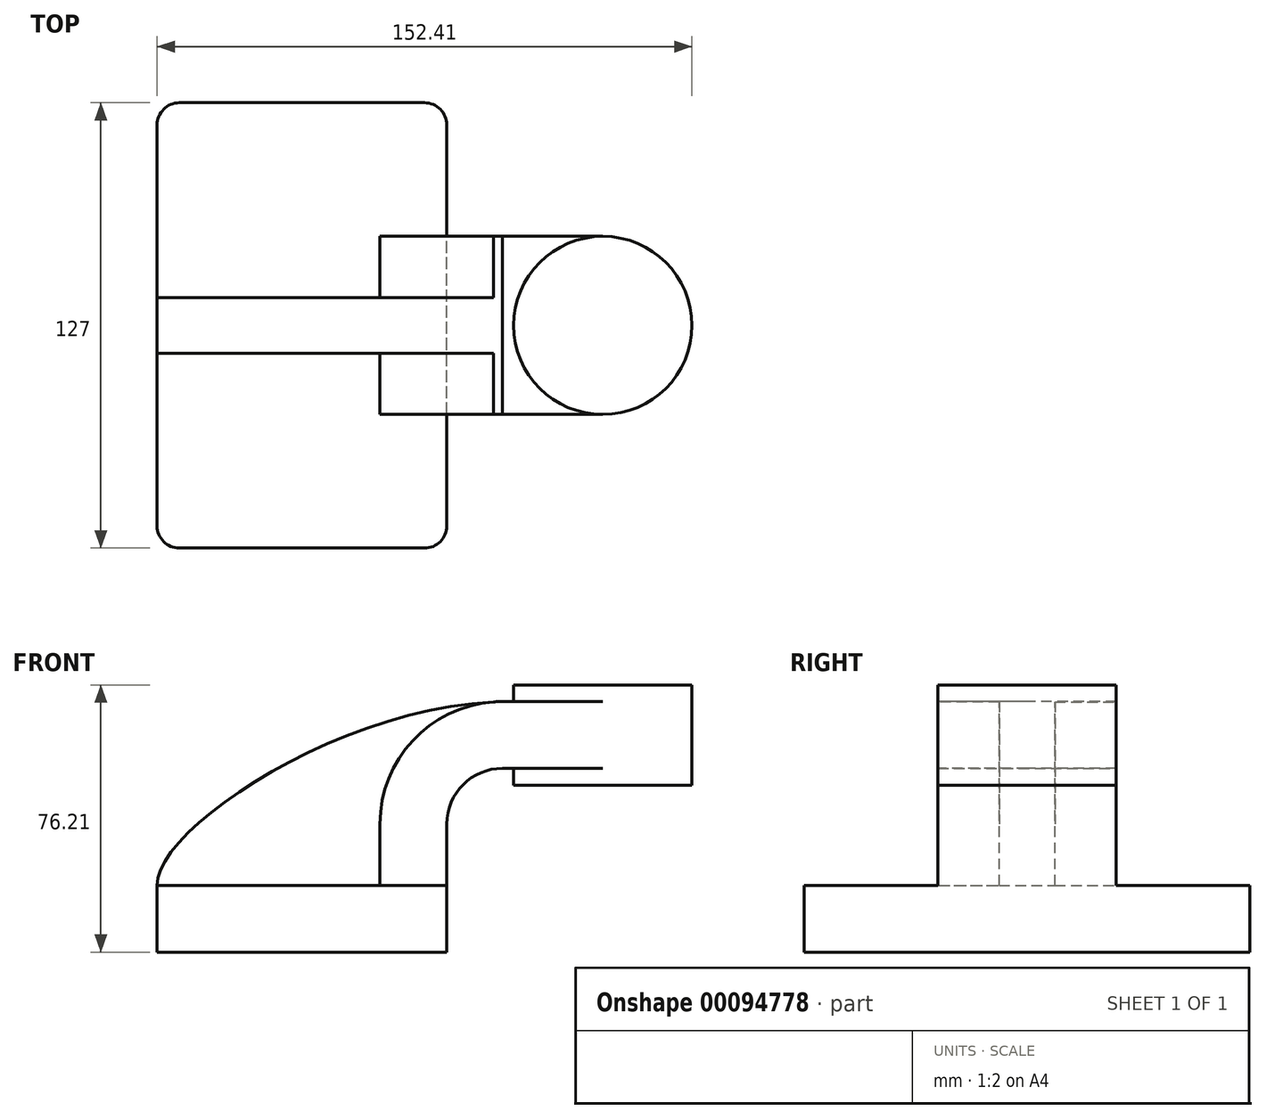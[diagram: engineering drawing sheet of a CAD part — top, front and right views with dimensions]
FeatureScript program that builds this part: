
annotation { "Feature Type Name" : "Feature", "Feature Type Description" : "" }
export const myFeature = defineFeature(function(context is Context, id is Id, definition is map)
    precondition{}
    {
        {
            var Q0;
            Q0=qCreatedBy(makeId("Front.planeOp"),FACE);
            var sketch = newSketch(context, id + "F0", { "sketchPlane" : qUnion([Q0])});
            skLineSegment(sketch, "E0.bottom", {"start": v(-41.27, -9.53) * mm, "end": v(41.28, -9.53) * mm});
            skLineSegment(sketch, "E0.top", {"start": v(-41.28, 9.52) * mm, "end": v(41.28, 9.52) * mm});
            skLineSegment(sketch, "E0.left", {"start": v(-41.28, -9.53) * mm, "end": v(-41.28, 9.52) * mm});
            skLineSegment(sketch, "E0.right", {"start": v(41.28, -9.53) * mm, "end": v(41.28, 9.52) * mm});
            skPoint(sketch, "E0.middle", {"position": v(0, 0) * mm});
            skLineSegment(sketch, "E1.bottom", {"start": v(60.32, 66.67) * mm, "end": v(111.12, 66.67) * mm});
            skLineSegment(sketch, "E1.top", {"start": v(60.33, 38.1) * mm, "end": v(111.12, 38.1) * mm});
            skLineSegment(sketch, "E1.left", {"start": v(60.32, 66.67) * mm, "end": v(60.32, 38.1) * mm});
            skLineSegment(sketch, "E1.right", {"start": v(111.12, 66.67) * mm, "end": v(111.12, 38.1) * mm});
            skPoint(sketch, "E1.middle", {"position": v(85.72, 52.39) * mm});
            skLineSegment(sketch, "E2", {"start": v(41.28, 9.52) * mm, "end": v(41.28, 27) * mm});
            skArc(sketch, "E3", {"start": v(41.27, 27) * mm, "mid": v(45.92, 38.23) * mm, "end": v(57.15, 42.88) * mm});
            skLineSegment(sketch, "E4", {"start": v(57.15, 42.88) * mm, "end": v(71.66, 42.88) * mm});
            skLineSegment(sketch, "E5.0", {"start": v(57.15, 61.93) * mm, "end": v(71.66, 61.93) * mm});
            skArc(sketch, "E5.1", {"start": v(22.22, 27) * mm, "mid": v(32.45, 51.7) * mm, "end": v(57.15, 61.93) * mm});
            skLineSegment(sketch, "E5.2", {"start": v(22.22, 9.52) * mm, "end": v(22.22, 27) * mm});
            skLineSegment(sketch, "E6", {"start": v(85.72, 38.1) * mm, "end": v(85.72, 66.67) * mm});
            skLineSegment(sketch, "E7", {"start": v(71.66, 61.93) * mm, "end": v(85.72, 61.93) * mm});
            skLineSegment(sketch, "E8", {"start": v(71.66, 42.88) * mm, "end": v(85.72, 42.88) * mm});
            skFitSpline(sketch, "E9", {"points": [v(-41.27, 9.53) * mm, v(57.15, 61.93) * mm], "startDerivative": vector(-2.18, 46.66) * mm, "endDerivative": vector(141.12, 3.38) * mm});
            skSolve(sketch);
        }
        {
            var Q0;
            Q0=makeQuery(id+"F0.imprint","IMPRINT",FACE,{"disambiguationData":[TD([[makeQuery(id+"F0.imprint","IMPRINT",EDGE,{"derivedFrom":sQuery(id+"F0.wireOp",EDGE,"E0.bottom")}),1.0]])]});
            extrude(context, id + "F1", {"entities" : qUnion([Q0]), "endBound" : BoundingType.SYMMETRIC, "depth" : 127 * mm});
        }
        {
            var Q0;
            {var subQ1=sQuery(id+"F0.wireOp",EDGE,"E2");Q0=makeQuery(id+"F0.imprint","IMPRINT",FACE,{"disambiguationData":[TD([[makeQuery(id+"F0.imprint","IMPRINT",EDGE,{"derivedFrom":subQ1}),1.0]])]});}
            extrude(context, id + "F2", {"entities" : qUnion([Q0]), "operationType" : NewBodyOperationType.ADD, "endBound" : BoundingType.SYMMETRIC, "depth" : 50.8 * mm});
        }
        {
            var Q0;
            {var subQ3=sQuery(id+"F0.wireOp",EDGE,"E5.2");Q0=makeQuery(id+"F0.imprint","IMPRINT",FACE,{"disambiguationData":[TD([[makeQuery(id+"F0.imprint","IMPRINT",EDGE,{"derivedFrom":subQ3}),1.0]])]});}
            extrude(context, id + "F3", {"entities" : qUnion([Q0]), "operationType" : NewBodyOperationType.ADD, "endBound" : BoundingType.SYMMETRIC, "depth" : 15.88 * mm});
        }
        {
            var Q0;
            {var subQ0=sQuery(id+"F0.wireOp",EDGE,"E7");Q0=makeQuery(id+"F0.imprint","IMPRINT",FACE,{"disambiguationData":[TD([[makeQuery(id+"F0.imprint","IMPRINT",EDGE,{"derivedFrom":subQ0}),-1.0]])]});}
            extrude(context, id + "F4", {"entities" : qUnion([Q0]), "operationType" : NewBodyOperationType.ADD, "endBound" : BoundingType.SYMMETRIC, "depth" : 50.8 * mm});
        }
        {
            var Q0;
            {var subQ0=sQuery(id+"F0.wireOp",EDGE,"E1.right");Q0=makeQuery(id+"F0.imprint","IMPRINT",FACE,{"disambiguationData":[TD([[makeQuery(id+"F0.imprint","IMPRINT",EDGE,{"derivedFrom":subQ0}),-1.0]])]});}
            var Q1;
            Q1=sQuery(id+"F0.wireOp",EDGE,"E6");
            revolve(context, id + "F5", {"operationType" : NewBodyOperationType.ADD, "entities" : qUnion([Q0]), "axis" : qUnion([Q1]), "revolveType" : RevolveType.FULL});
        }
        {
            var Q0;
            Q0=makeQuery(id+"F1.opExtrude","CAP_EDGE",EDGE,{"disambiguationData":[OSD([sQuery(id+"F0.wireOp",EDGE,"E0.right")])],"isStart":false});
            var Q1;
            Q1=makeQuery(id+"F1.opExtrude","CAP_EDGE",EDGE,{"disambiguationData":[OSD([sQuery(id+"F0.wireOp",EDGE,"E0.left")])],"isStart":false});
            var Q2;
            Q2=makeQuery(id+"F1.opExtrude","CAP_EDGE",EDGE,{"disambiguationData":[OSD([sQuery(id+"F0.wireOp",EDGE,"E0.right")])],"isStart":true});
            var Q3;
            Q3=makeQuery(id+"F1.opExtrude","CAP_EDGE",EDGE,{"disambiguationData":[OSD([sQuery(id+"F0.wireOp",EDGE,"E0.left")])],"isStart":true});
            fillet(context, id + "F6", {"entities" : qUnion([Q0, Q1, Q2, Q3]), "radius" : 6.35 * mm, "tangentPropagation" : true, "allowEdgeOverflow" : false});
        }
    });
